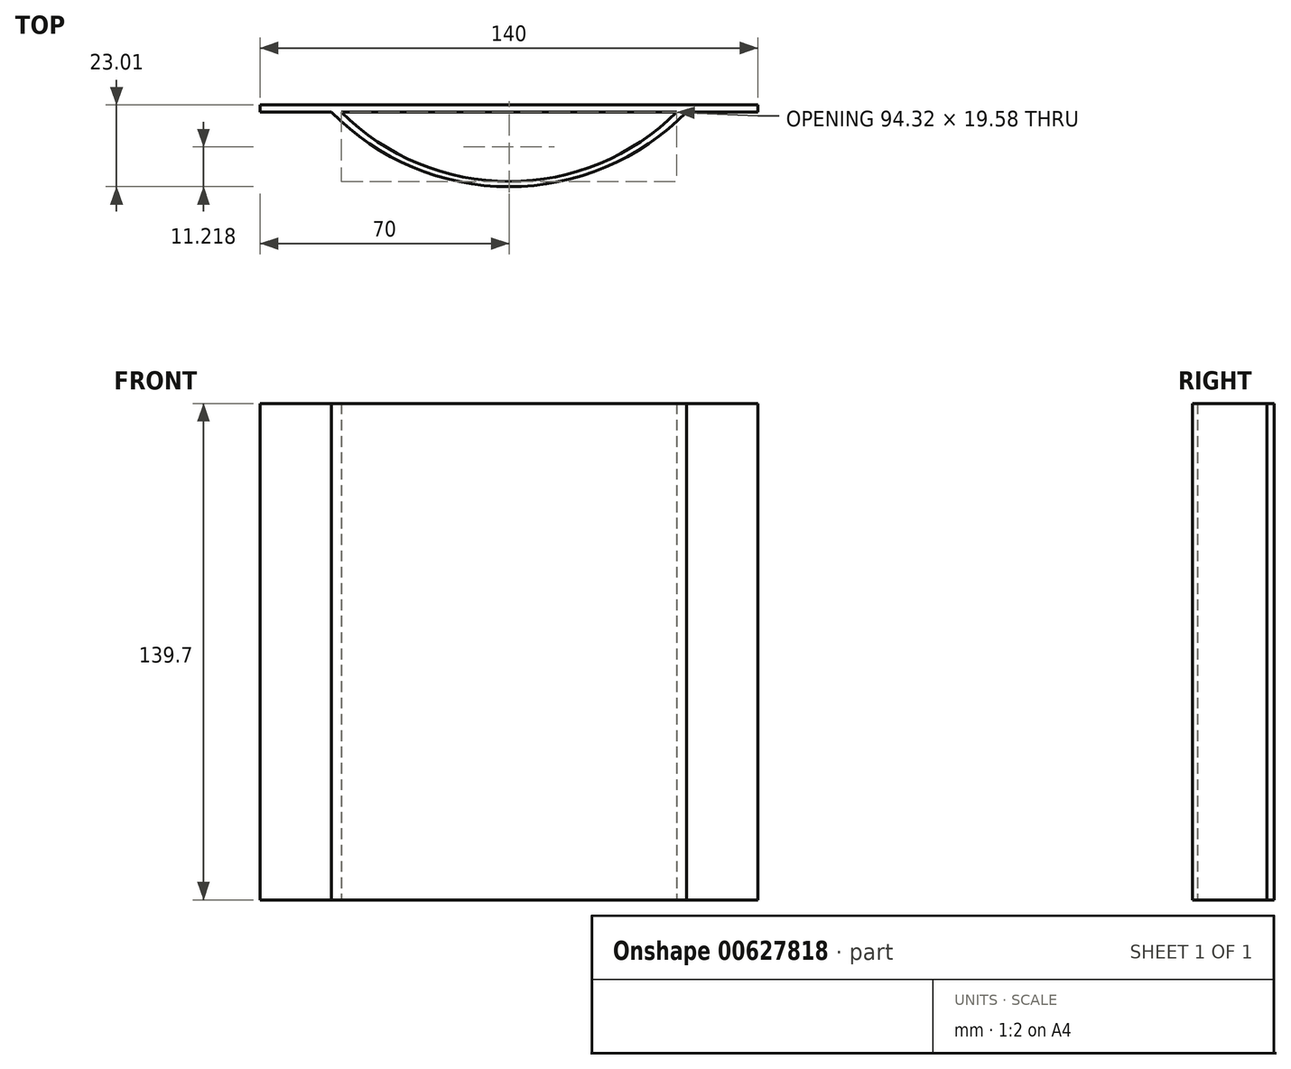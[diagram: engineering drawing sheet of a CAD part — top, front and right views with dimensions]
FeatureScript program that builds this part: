
annotation { "Feature Type Name" : "Feature", "Feature Type Description" : "" }
export const myFeature = defineFeature(function(context is Context, id is Id, definition is map)
    precondition{}
    {
        {
            var Q0;
            Q0=qCreatedBy(makeId("Top.planeOp"),FACE);
            var sketch = newSketch(context, id + "F0", { "sketchPlane" : qUnion([Q0])});
            skLineSegment(sketch, "E0", {"start": v(50, 0) * mm, "end": v(-50, 0) * mm, "construction": true});
            skPoint(sketch, "E1", {"position": v(0, 0) * mm});
            skArc(sketch, "E2", {"start": v(-50, 0) * mm, "mid": v(0, -21.01) * mm, "end": v(50, 0) * mm});
            skLineSegment(sketch, "E3", {"start": v(0, 0) * mm, "end": v(0, 2) * mm, "construction": true});
            skLineSegment(sketch, "E4", {"start": v(-70, 2) * mm, "end": v(70, 2) * mm});
            skPoint(sketch, "E5", {"position": v(0, 2) * mm});
            skLineSegment(sketch, "E6", {"start": v(-70, 2) * mm, "end": v(-70, 0) * mm});
            skLineSegment(sketch, "E7", {"start": v(-70, 0) * mm, "end": v(-50, 0) * mm});
            skLineSegment(sketch, "E8", {"start": v(70, 2) * mm, "end": v(70, 0) * mm});
            skLineSegment(sketch, "E9", {"start": v(70, 0) * mm, "end": v(50, 0) * mm});
            skLineSegment(sketch, "E10", {"start": v(0, 48.99) * mm, "end": v(0, 46.99) * mm, "construction": true});
            skArc(sketch, "E11", {"start": v(-47.16, 0) * mm, "mid": v(0, -19.58) * mm, "end": v(47.16, 0) * mm});
            skLineSegment(sketch, "E12", {"start": v(-47.16, 0) * mm, "end": v(47.16, 0) * mm});
            skSolve(sketch);
        }
        {
            var Q0;
            Q0 = qSketchRegion(id + "F0", true);
            extrude(context, id + "F1", {"entities" : qUnion([Q0]), "endBound" : BoundingType.SYMMETRIC, "depth" : 139.7 * mm, "offsetDistance" : 25 * mm});
        }
    });
